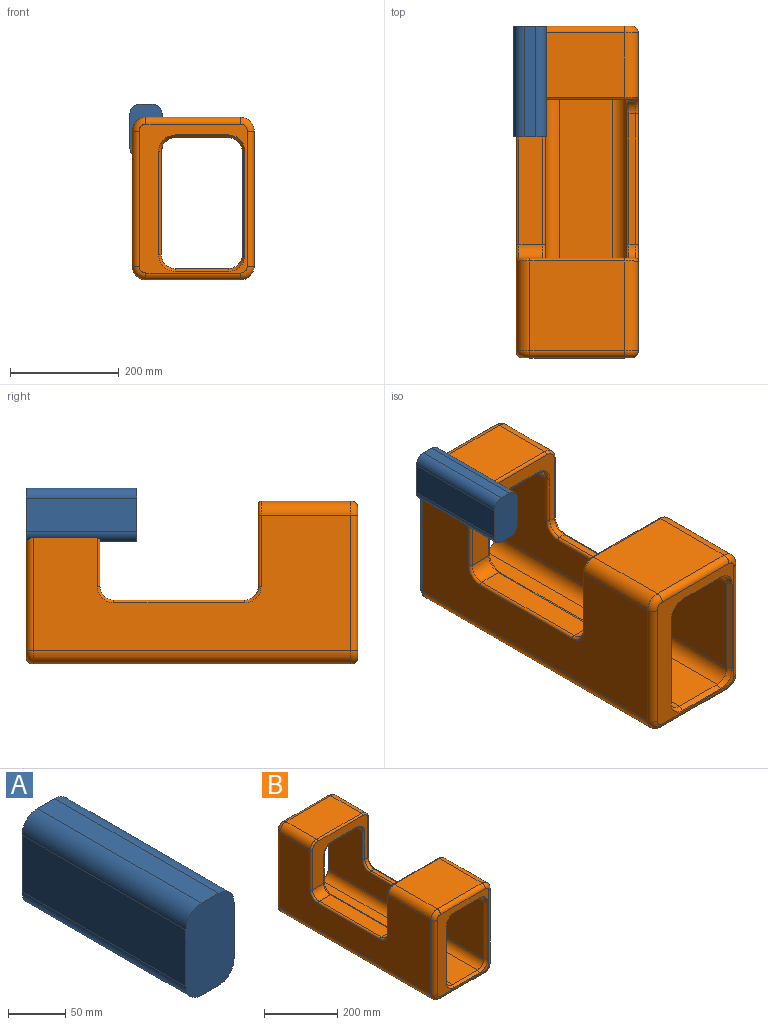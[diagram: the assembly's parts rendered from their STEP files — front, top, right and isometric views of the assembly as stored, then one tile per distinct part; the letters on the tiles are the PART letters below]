
ASSEMBLY  parts=2 mates=1
PART A: 10 faces, bbox 59.5x203.2x99 mm
  f0: plane 203.2x60.87mm, normal (-1,0,0), area 12369.3mm2, adj f4,f5,f6,f9
  f1: plane 203.2x21.42mm, normal (0,0,-1), area 4353.4mm2, adj f4,f5,f6,f7
  f2: plane 203.2x60.87mm, normal (1,0,0), area 12369.3mm2, adj f4,f5,f7,f8
  f3: plane 203.2x21.42mm, normal (0,0,1), area 4353.4mm2, adj f4,f5,f8,f9
  f4: plane 98.97x59.52mm, normal (0,-1,0), area 5579.8mm2, adj f0,f1,f2,f3,f6,f7,f8,f9
  f5: plane 98.97x59.52mm, normal (0,1,0), area 5579.8mm2, adj f0,f1,f2,f3,f6,f7,f8,f9
  f6: cylinder r=19.05mm len=203.2mm, axis (0,1,0), area 6080.5mm2, adj f0,f1,f4,f5
  f7: cylinder r=19.05mm len=203.2mm, axis (0,-1,0), area 6080.5mm2, adj f1,f2,f4,f5
  f8: cylinder r=19.05mm len=203.2mm, axis (0,1,0), area 6080.5mm2, adj f2,f3,f4,f5
  f9: cylinder r=19.05mm len=203.2mm, axis (0,-1,0), area 6080.5mm2, adj f0,f3,f4,f5
PART B: 88 faces, bbox 228.5x609.6x303.3 mm
  f0: plane 173.5x165.08mm, normal (0,0,1), area 28640.9mm2, adj f5,f6,f24,f56
  f1: plane 584.2x248.29mm, normal (-1,0,0), area 96797mm2, adj f5,f20,f21,f27,f35,f48,f49,f50
  f2: plane 130.64x97.82mm, normal (0,0,-1), area 12778.8mm2, adj f3,f4,f15,f72
  f3: cylinder r=25.4mm len=130.64mm, axis (0,-1,0), area 5212.3mm2, adj f2,f10,f15,f74
  f4: cylinder r=25.4mm len=130.64mm, axis (0,1,0), area 5212.3mm2, adj f2,f12,f15,f70
  f5: cylinder r=25.4mm len=165.08mm, axis (0,1,0), area 6586.3mm2, adj f0,f1,f25,f54
  f6: cylinder r=25.4mm len=165.08mm, axis (0,-1,0), area 6586.3mm2, adj f0,f13,f26,f58
  f7: plane 173.5x117.94mm, normal (0,0,1), area 20462.2mm2, adj f20,f23,f32,f55
  f8: plane 584.2x173.5mm, normal (0,0,-1), area 101357.7mm2, adj f21,f22,f31,f39
  f9: plane 168.98x97.82mm, normal (0,0,-1), area 16529.2mm2, adj f16,f19,f71,f87
  f10: plane 600.8x189.64mm, normal (-1,0,0), area 77049.8mm2, adj f3,f15,f16,f17,f75,f76,f77,f78
  f11: plane 600.8x97.82mm, normal (0,0,1), area 58769mm2, adj f15,f17,f18,f80
  f12: plane 600.8x189.64mm, normal (1,0,0), area 77049.8mm2, adj f4,f15,f18,f19,f64,f65,f66,f67
  f13: plane 584.2x248.29mm, normal (1,0,0), area 96797mm2, adj f6,f22,f23,f28,f36,f59,f60,f61
  f14: plane 273.69x198.9mm, normal (0,-1,0), area 15306.6mm2, adj f24,f25,f26,f27,f28,f29,f30,f31
  f15: plane 273.69x198.9mm, normal (0,1,0), area 19119mm2, adj f2,f3,f4,f10,f11,f12,f17,f18
  f16: cylinder r=25.4mm len=168.98mm, axis (0,-1,0), area 6742mm2, adj f9,f10,f73,f85
  f17: cylinder r=25.4mm len=600.8mm, axis (0,1,0), area 23970.9mm2, adj f10,f11,f15,f81
  f18: cylinder r=25.4mm len=600.8mm, axis (0,-1,0), area 23970.9mm2, adj f11,f12,f15,f82
  f19: cylinder r=25.4mm len=168.98mm, axis (0,1,0), area 6742mm2, adj f9,f12,f69,f86
  f20: cylinder r=25.4mm len=117.94mm, axis (0,1,0), area 4705.5mm2, adj f1,f7,f33,f53
  f21: cylinder r=25.4mm len=584.2mm, axis (0,-1,0), area 23308.5mm2, adj f1,f8,f29,f37
  f22: cylinder r=25.4mm len=584.2mm, axis (0,1,0), area 23308.5mm2, adj f8,f13,f30,f38
  f23: cylinder r=25.4mm len=117.94mm, axis (0,-1,0), area 4705.5mm2, adj f7,f13,f34,f57
  f24: cylinder r=12.7mm len=173.5mm, axis (1,0,0), area 3461.1mm2, adj f0,f14,f25,f26
  f25: torus R=12.7mm, axis (0,-1,0), area 651.3mm2, adj f5,f14,f24,f27
  f26: torus R=12.7mm, axis (0,-1,0), area 651.3mm2, adj f6,f14,f24,f28
  f27: cylinder r=12.7mm len=248.29mm, axis (0,0,1), area 4953.2mm2, adj f1,f14,f25,f29
  f28: cylinder r=12.7mm len=248.29mm, axis (0,0,-1), area 4953.2mm2, adj f13,f14,f26,f30
  f29: torus R=12.7mm, axis (0,-1,0), area 651.3mm2, adj f14,f21,f27,f31
  f30: torus R=12.7mm, axis (0,-1,0), area 651.3mm2, adj f14,f22,f28,f31
  f31: cylinder r=12.7mm len=173.5mm, axis (-1,0,0), area 3461.1mm2, adj f8,f14,f29,f30
  f32: cylinder r=12.7mm len=173.5mm, axis (-1,0,0), area 3461.1mm2, adj f7,f15,f33,f34
  f33: torus R=12.7mm, axis (0,-1,0), area 651.3mm2, adj f15,f20,f32,f35
  f34: torus R=12.7mm, axis (0,-1,0), area 651.3mm2, adj f15,f23,f32,f36
  f35: cylinder r=12.7mm len=248.29mm, axis (0,0,-1), area 4953.2mm2, adj f1,f15,f33,f37
  f36: cylinder r=12.7mm len=248.29mm, axis (0,0,1), area 4953.2mm2, adj f13,f15,f34,f38
  f37: torus R=12.7mm, axis (0,-1,0), area 651.3mm2, adj f15,f21,f35,f39
  f38: torus R=12.7mm, axis (0,-1,0), area 651.3mm2, adj f15,f22,f36,f39
  f39: cylinder r=12.7mm len=173.5mm, axis (1,0,0), area 3461.1mm2, adj f8,f15,f37,f38
  f40: plane 240.22x43.49mm, normal (0,0,1), area 10448.3mm2, adj f46,f47,f48,f64
  f41: plane 240.22x11.87mm, normal (0,0,1), area 2850.6mm2, adj f44,f45,f63,f79
  f42: plane 214.14x151.38mm, normal (0,1,0), area 12983.3mm2, adj f44,f46,f52,f54,f56,f58,f60,f67
  f43: plane 214.14x151.38mm, normal (0,-1,0), area 12983.3mm2, adj f45,f47,f51,f53,f55,f57,f59,f68
  f44: cylinder r=25.4mm len=25.4mm, axis (1,0,0), area 473.5mm2, adj f41,f42,f62,f77
  f45: cylinder r=25.4mm len=25.4mm, axis (-1,0,0), area 473.5mm2, adj f41,f43,f61,f78
  f46: cylinder r=25.4mm len=43.49mm, axis (1,0,0), area 1735.3mm2, adj f40,f42,f50,f65
  f47: cylinder r=25.4mm len=43.49mm, axis (-1,0,0), area 1735.3mm2, adj f40,f43,f49,f66
  f48: cylinder r=5.08mm len=240.22mm, axis (0,-1,0), area 1916.9mm2, adj f1,f40,f49,f50
  f49: torus R=30.48mm, axis (-1,0,0), area 341.5mm2, adj f1,f47,f48,f51
  f50: torus R=30.48mm, axis (-1,0,0), area 341.5mm2, adj f1,f46,f48,f52
  f51: cylinder r=5.08mm len=131.06mm, axis (0,0,-1), area 1045.8mm2, adj f1,f43,f49,f53
  f52: cylinder r=5.08mm len=131.06mm, axis (0,0,1), area 1045.8mm2, adj f1,f42,f50,f54
  f53: torus R=20.32mm, axis (0,-1,0), area 295.2mm2, adj f20,f43,f51,f55
  f54: torus R=20.32mm, axis (0,-1,0), area 295.2mm2, adj f5,f42,f52,f56
  f55: cylinder r=5.08mm len=173.5mm, axis (-1,0,0), area 1384.5mm2, adj f7,f43,f53,f57
  f56: cylinder r=5.08mm len=173.5mm, axis (1,0,0), area 1384.5mm2, adj f0,f42,f54,f58
  f57: torus R=20.32mm, axis (0,-1,0), area 295.2mm2, adj f23,f43,f55,f59
  f58: torus R=20.32mm, axis (0,-1,0), area 295.2mm2, adj f6,f42,f56,f60
  f59: cylinder r=5.08mm len=131.06mm, axis (0,0,1), area 1045.8mm2, adj f13,f43,f57,f61
  f60: cylinder r=5.08mm len=131.06mm, axis (0,0,-1), area 1045.8mm2, adj f13,f42,f58,f62
  f61: torus R=30.48mm, axis (-1,0,0), area 341.5mm2, adj f13,f45,f59,f63
  f62: torus R=30.48mm, axis (-1,0,0), area 341.5mm2, adj f13,f44,f60,f63
  f63: cylinder r=5.08mm len=240.22mm, axis (0,1,0), area 1916.9mm2, adj f13,f41,f61,f62
  f64: cylinder r=5.08mm len=240.22mm, axis (0,-1,0), area 1916.9mm2, adj f12,f40,f65,f66
  f65: torus R=30.48mm, axis (-1,0,0), area 341.5mm2, adj f12,f46,f64,f67
  f66: torus R=30.48mm, axis (-1,0,0), area 341.5mm2, adj f12,f47,f64,f68
  f67: cylinder r=5.08mm len=93.31mm, axis (0,0,1), area 744.6mm2, adj f12,f42,f65,f69
  f68: cylinder r=5.08mm len=93.31mm, axis (0,0,-1), area 744.6mm2, adj f12,f43,f66,f70
  f69: torus R=30.48mm, axis (0,-1,0), area 341.5mm2, adj f19,f42,f67,f71
  f70: torus R=30.48mm, axis (0,-1,0), area 341.5mm2, adj f4,f43,f68,f72
  f71: cylinder r=5.08mm len=97.82mm, axis (1,0,0), area 780.6mm2, adj f9,f42,f69,f73
  f72: cylinder r=5.08mm len=97.82mm, axis (-1,0,0), area 780.6mm2, adj f2,f43,f70,f74
  f73: torus R=30.48mm, axis (0,-1,0), area 341.5mm2, adj f16,f42,f71,f75
  f74: torus R=30.48mm, axis (0,-1,0), area 341.5mm2, adj f3,f43,f72,f76
  f75: cylinder r=5.08mm len=93.31mm, axis (0,0,-1), area 744.6mm2, adj f10,f42,f73,f77
  f76: cylinder r=5.08mm len=93.31mm, axis (0,0,1), area 744.6mm2, adj f10,f43,f74,f78
  f77: torus R=30.48mm, axis (-1,0,0), area 341.5mm2, adj f10,f44,f75,f79
  f78: torus R=30.48mm, axis (-1,0,0), area 341.5mm2, adj f10,f45,f76,f79
  f79: cylinder r=5.08mm len=240.22mm, axis (0,1,0), area 1916.9mm2, adj f10,f41,f77,f78
  f80: plane 97.82x8.8mm, normal (0,-0.5,0.87), area 993.8mm2, adj f11,f14,f81,f82
  f81: cone r=30.48mm half-angle=30deg, axis (0,-1,0), area 445.9mm2, adj f14,f17,f80,f83
  f82: cone r=30.48mm half-angle=30deg, axis (0,-1,0), area 445.9mm2, adj f14,f18,f80,f84
  f83: plane 189.64x8.8mm, normal (-0.87,-0.5,0), area 1926.7mm2, adj f10,f14,f81,f85
  f84: plane 189.64x8.8mm, normal (0.87,-0.5,0), area 1926.7mm2, adj f12,f14,f82,f86
  f85: cone r=30.48mm half-angle=30deg, axis (0,-1,0), area 445.9mm2, adj f14,f16,f83,f87
  f86: cone r=30.48mm half-angle=30deg, axis (0,-1,0), area 445.9mm2, adj f14,f19,f84,f87
  f87: plane 97.82x8.8mm, normal (0,-0.5,-0.87), area 993.8mm2, adj f9,f14,f85,f86
PLACE A t=(34.63,0,159.9)mm
PLACE B at identity
MATE parallel A.f5 <-> B.f5  axis (0,1,0) through (64.39,0,156.46)mm
